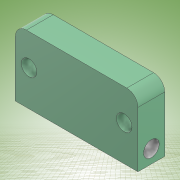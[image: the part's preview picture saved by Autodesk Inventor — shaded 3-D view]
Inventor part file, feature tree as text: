
AUTODESK INVENTOR PART (.ipt)
format: ipt  version: 2022 (Build 260153000, 153)  size: 149,504 bytes
history: native  units: mm
features: extrude x3, sketch x3, other x1, fillet x1
ambient origin geometry x8: Origin, YZ Plane, XZ Plane, XY Plane, X Axis, Y Axis, Z Axis, Center Point
bodies: Body1 (feature_tree)
feature tree (8):
  other  "Sólido1"
  extrude  "Extrusión1"  Depth=55.0mm
  fillet  "Empalme1"  Radius=20.0mm
  extrude  "Extrusión5"  Depth=5.0mm
  extrude  "Extrusión6"  Depth=10.0mm TaperAngle=0.0deg
  sketch  "Boceto1"  dims[d0=7.0mm d1=55.0mm d3=20.0mm]
  sketch  "Boceto7"  dims[d4=12.0mm d5=0.0mm d15=5.0mm]
  sketch  "Boceto8"  dims[d23=42.67mm d24=10.0mm d25=0.0mm d26=7.0mm d27=6.0mm d29=55.0mm d30=0.0mm d31=6.0mm]
